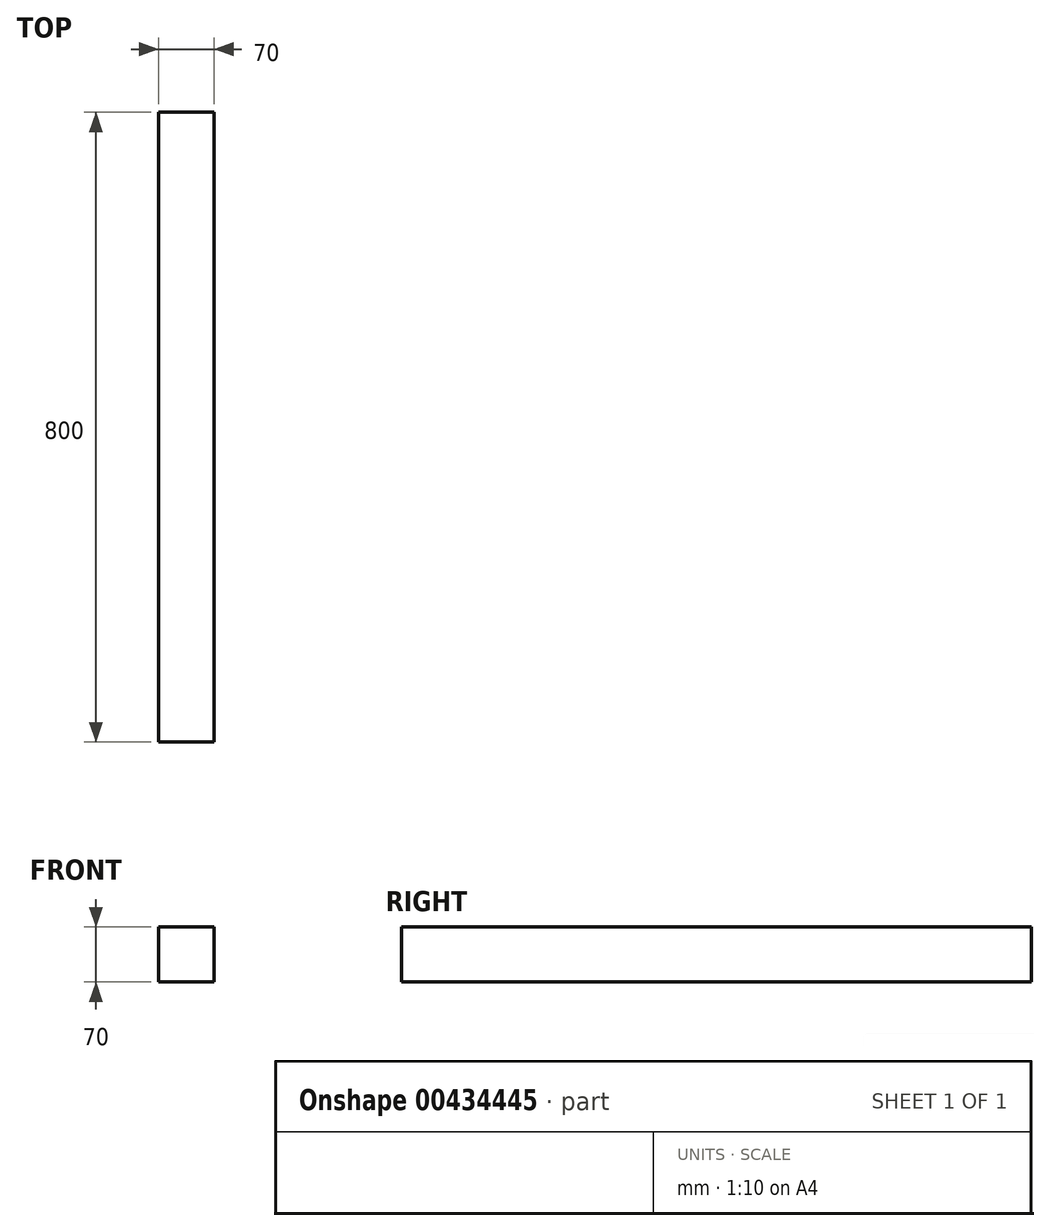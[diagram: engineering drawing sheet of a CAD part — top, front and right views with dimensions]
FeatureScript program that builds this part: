
annotation { "Feature Type Name" : "Feature", "Feature Type Description" : "" }
export const myFeature = defineFeature(function(context is Context, id is Id, definition is map)
    precondition{}
    {
        {
            var Q0;
            Q0=qCreatedBy(makeId("Front.planeOp"),FACE);
            var sketch = newSketch(context, id + "F0", { "sketchPlane" : qUnion([Q0])});
            skLineSegment(sketch, "E0.bottom", {"start": v(35, 35) * mm, "end": v(-35, 35) * mm});
            skLineSegment(sketch, "E0.top", {"start": v(35, -35) * mm, "end": v(-35, -35) * mm});
            skLineSegment(sketch, "E0.left", {"start": v(35, 35) * mm, "end": v(35, -35) * mm});
            skLineSegment(sketch, "E0.right", {"start": v(-35, 35) * mm, "end": v(-35, -35) * mm});
            skPoint(sketch, "E0.middle", {"position": v(0, 0) * mm});
            skSolve(sketch);
        }
        {
            var Q0;
            Q0 = qSketchRegion(id + "F0", true);
            extrude(context, id + "F1", {"entities" : qUnion([Q0]), "depth" : 800 * mm, "offsetDistance" : 25 * mm});
        }
    });
